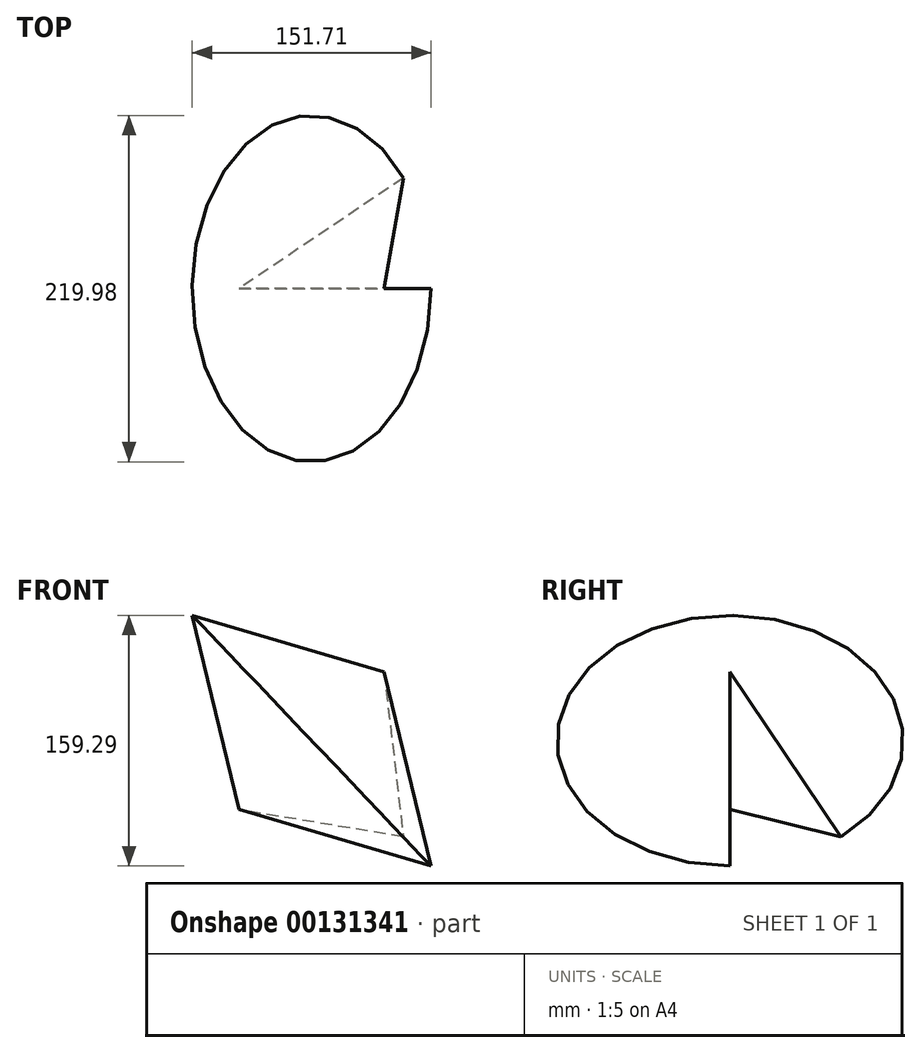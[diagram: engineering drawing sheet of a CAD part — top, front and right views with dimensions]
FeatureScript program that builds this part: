
annotation { "Feature Type Name" : "Feature", "Feature Type Description" : "" }
export const myFeature = defineFeature(function(context is Context, id is Id, definition is map)
    precondition{}
    {
        {
            var Q0;
            Q0=qCreatedBy(makeId("Front.planeOp"),FACE);
            var sketch = newSketch(context, id + "F0", { "sketchPlane" : qUnion([Q0])});
            skCircle(sketch, "E0.cCircle", {"center": v(0, 0) * mm, "radius": 36.66 * mm, "construction": true});
            skLineSegment(sketch, "E0.0", {"start": v(-71.27, -17.24) * mm, "end": v(20.7, 70.34) * mm});
            skLineSegment(sketch, "E0.1", {"start": v(20.7, 70.34) * mm, "end": v(50.57, -53.1) * mm});
            skLineSegment(sketch, "E0.2", {"start": v(50.57, -53.1) * mm, "end": v(-71.27, -17.24) * mm});
            skPoint(sketch, "E0.0.midPoint", {"position": v(-25.28, 26.55) * mm});
            skSolve(sketch);
        }
        {
            var Q0;
            Q0=makeQuery(id+"F0.imprint","IMPRINT",FACE,{"disambiguationData":[TD([[makeQuery(id+"F0.imprint","IMPRINT",EDGE,{"derivedFrom":sQuery(id+"F0.wireOp",EDGE,"E0.0")}),-1.0]])]});
            var Q1;
            Q1=sQuery(id+"F0.wireOp",EDGE,"E0.0");
            revolve(context, id + "F1", {"entities" : qUnion([Q0]), "axis" : qUnion([Q1]), "revolveType" : RevolveType.ONE_DIRECTION, "oppositeDirection" : true, "angle" : 320.25 * degree});
        }
    });
